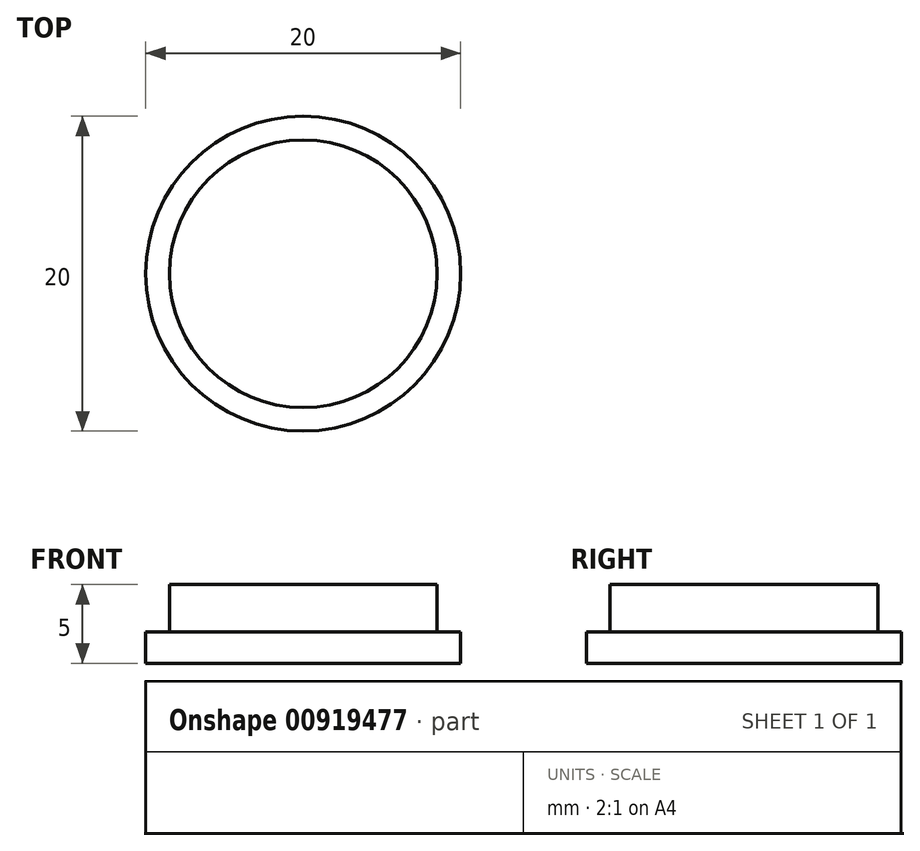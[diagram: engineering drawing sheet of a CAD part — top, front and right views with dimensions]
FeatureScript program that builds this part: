
annotation { "Feature Type Name" : "Feature", "Feature Type Description" : "" }
export const myFeature = defineFeature(function(context is Context, id is Id, definition is map)
    precondition{}
    {
        {
            var Q0;
            Q0=qCreatedBy(makeId("Top.planeOp"),FACE);
            var sketch = newSketch(context, id + "F0", { "sketchPlane" : qUnion([Q0])});
            skCircle(sketch, "E0", {"center": v(0, 0) * mm, "radius": 10 * mm});
            skSolve(sketch);
        }
        {
            var Q0;
            Q0=qSketchRegion(id+"F0",true);
            extrude(context, id + "F1", {"entities" : qUnion([Q0]), "depth" : 5 * mm, "offsetDistance" : 25 * mm, "symmetric" : true});
        }
        {
            var Q0;
            Q0=makeQuery(id+"F1.opExtrude","CAP_FACE",FACE,{"disambiguationData":[OSD([sQuery(id+"F0.wireOp",EDGE,"E0")])],"isStart":false});
            var sketch = newSketch(context, id + "F2", { "sketchPlane" : qUnion([Q0])});
            skCircle(sketch, "E1", {"center": v(0, 0) * mm, "radius": 10 * mm});
            skCircle(sketch, "E2.0", {"center": v(0, 0) * mm, "radius": 8.5 * mm});
            skSolve(sketch);
        }
        {
            var Q0;
            Q0=qSketchRegion(id+"F2",true);
            extrude(context, id + "F3", {"entities" : qUnion([Q0]), "operationType" : NewBodyOperationType.REMOVE, "oppositeDirection" : true, "depth" : 3 * mm, "offsetDistance" : 25 * mm});
        }
    });
